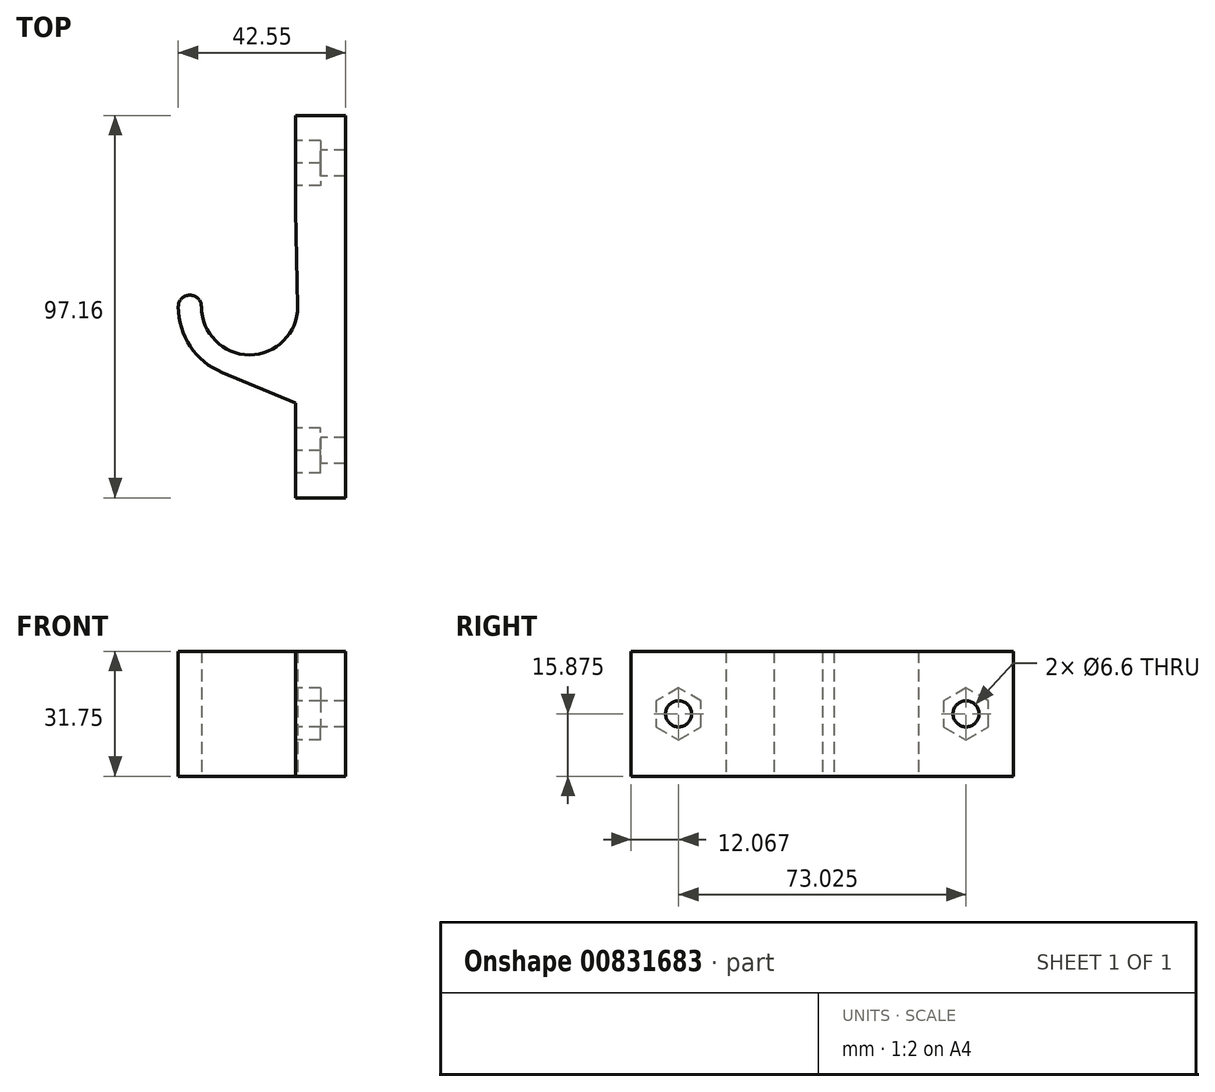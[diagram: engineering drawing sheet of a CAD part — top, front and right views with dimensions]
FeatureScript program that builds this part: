
annotation { "Feature Type Name" : "Feature", "Feature Type Description" : "" }
export const myFeature = defineFeature(function(context is Context, id is Id, definition is map)
    precondition{}
    {
        {
            assignVariable(context, id + "F0", {"name" : "materialThickness", "anyValue" : 6.35 * mm});
        }
        {
            assignVariable(context, id + "F1", {"name" : "overallThickness", "anyValue" : 31.75 * mm});
        }
        {
            var Q0;
            Q0=qCreatedBy(makeId("Top.planeOp"),FACE);
            var sketch = newSketch(context, id + "F2", { "sketchPlane" : qUnion([Q0])});
            skCircle(sketch, "E0", {"center": v(0, 0) * mm, "radius": 11.75 * mm, "construction": true});
            skLineSegment(sketch, "E1", {"start": v(0, 0) * mm, "end": v(24.45, 0) * mm, "construction": true});
            skLineSegment(sketch, "E2", {"start": v(24.45, 48.58) * mm, "end": v(24.45, -48.58) * mm});
            skLineSegment(sketch, "E3", {"start": v(24.45, 48.58) * mm, "end": v(11.75, 48.58) * mm});
            skLineSegment(sketch, "E4", {"start": v(24.45, -48.58) * mm, "end": v(11.75, -48.58) * mm});
            skLineSegment(sketch, "E5", {"start": v(11.75, 48.58) * mm, "end": v(11.75, 24.45) * mm});
            skLineSegment(sketch, "E6", {"start": v(11.75, -48.58) * mm, "end": v(11.75, -24.45) * mm});
            skCircle(sketch, "E7", {"center": v(0, 0) * mm, "radius": 18.1 * mm, "construction": true});
            skLineSegment(sketch, "E8", {"start": v(11.75, -24.45) * mm, "end": v(-6.92, -16.73) * mm});
            skLineSegment(sketch, "E9", {"start": v(11.75, 24.45) * mm, "end": v(12.22, 0) * mm});
            skLineSegment(sketch, "E10", {"start": v(0, 0) * mm, "end": v(-18.1, 0) * mm, "construction": true});
            skArc(sketch, "E11", {"start": v(12.22, 0) * mm, "mid": v(0, -12.22) * mm, "end": v(-12.22, 0) * mm});
            skArc(sketch, "E12", {"start": v(-6.92, -16.73) * mm, "mid": v(-15.05, -10.06) * mm, "end": v(-18.1, 0) * mm});
            skArc(sketch, "E13", {"start": v(-12.22, 0) * mm, "mid": v(-15.16, 2.94) * mm, "end": v(-18.1, 0) * mm});
            skSolve(sketch);
        }
        {
            var Q0;
            Q0=makeQuery(id+"F2.imprint","IMPRINT",FACE,{"disambiguationData":[TD([[makeQuery(id+"F2.imprint","IMPRINT",EDGE,{"derivedFrom":sQuery(id+"F2.wireOp",EDGE,"E2")}),-1.0]])]});
            extrude(context, id + "F3", {"entities" : qUnion([Q0]), "depth" : getVariable(context, 'overallThickness'), "offsetDistance" : 25.4 * mm});
        }
        {
            var Q0;
            Q0=makeQuery(id+"F3.opExtrude","SWEPT_FACE",FACE,{"disambiguationData":[OSD([sQuery(id+"F2.wireOp",EDGE,"E5"),sQuery(id+"F2.wireOp",EDGE,"E9")])]});
            var sketch = newSketch(context, id + "F4", { "sketchPlane" : qUnion([Q0])});
            skLineSegment(sketch, "E14.0", {"start": v(-48.58, 31.75) * mm, "end": v(-24.45, 31.75) * mm, "construction": true});
            skLineSegment(sketch, "E15.0", {"start": v(-48.58, 31.75) * mm, "end": v(-48.58, 0) * mm, "construction": true});
            skLineSegment(sketch, "E16.0", {"start": v(-48.58, 0) * mm, "end": v(-24.45, 0) * mm, "construction": true});
            skLineSegment(sketch, "E17.0", {"start": v(48.58, 31.75) * mm, "end": v(24.45, 31.75) * mm, "construction": true});
            skLineSegment(sketch, "E18.0", {"start": v(48.58, 31.75) * mm, "end": v(48.58, 0) * mm, "construction": true});
            skLineSegment(sketch, "E19.0", {"start": v(48.58, 0) * mm, "end": v(24.45, 0) * mm, "construction": true});
            skLineSegment(sketch, "E20", {"start": v(-48.58, 15.88) * mm, "end": v(48.58, 15.88) * mm, "construction": true});
            skPoint(sketch, "E21", {"position": v(-36.51, 15.88) * mm});
            skPoint(sketch, "E22", {"position": v(36.51, 15.88) * mm});
            skCircle(sketch, "E23", {"center": v(36.51, 15.88) * mm, "radius": 3.3 * mm});
            skCircle(sketch, "E24", {"center": v(-36.51, 15.88) * mm, "radius": 3.3 * mm});
            skCircle(sketch, "E25.cCircle", {"center": v(-36.51, 15.88) * mm, "radius": 5.72 * mm, "construction": true});
            skLineSegment(sketch, "E25.0", {"start": v(-30.8, 19.17) * mm, "end": v(-30.8, 12.58) * mm});
            skLineSegment(sketch, "E25.1", {"start": v(-30.8, 12.58) * mm, "end": v(-36.51, 9.28) * mm});
            skLineSegment(sketch, "E25.2", {"start": v(-36.51, 9.28) * mm, "end": v(-42.23, 12.58) * mm});
            skLineSegment(sketch, "E25.3", {"start": v(-42.23, 12.58) * mm, "end": v(-42.23, 19.17) * mm});
            skLineSegment(sketch, "E25.4", {"start": v(-42.23, 19.17) * mm, "end": v(-36.51, 22.47) * mm});
            skLineSegment(sketch, "E25.5", {"start": v(-36.51, 22.47) * mm, "end": v(-30.8, 19.17) * mm});
            skPoint(sketch, "E25.0.midPoint", {"position": v(-30.8, 15.88) * mm});
            skCircle(sketch, "E26.cCircle", {"center": v(36.51, 15.88) * mm, "radius": 5.72 * mm, "construction": true});
            skLineSegment(sketch, "E26.0", {"start": v(30.8, 12.58) * mm, "end": v(30.8, 19.17) * mm});
            skLineSegment(sketch, "E26.1", {"start": v(30.8, 19.17) * mm, "end": v(36.51, 22.47) * mm});
            skLineSegment(sketch, "E26.2", {"start": v(36.51, 22.47) * mm, "end": v(42.23, 19.17) * mm});
            skLineSegment(sketch, "E26.3", {"start": v(42.23, 19.17) * mm, "end": v(42.23, 12.58) * mm});
            skLineSegment(sketch, "E26.4", {"start": v(42.23, 12.58) * mm, "end": v(36.51, 9.28) * mm});
            skLineSegment(sketch, "E26.5", {"start": v(36.51, 9.28) * mm, "end": v(30.8, 12.58) * mm});
            skPoint(sketch, "E26.0.midPoint", {"position": v(30.8, 15.88) * mm});
            skSolve(sketch);
        }
        {
            var Q0;
            Q0=makeQuery(id+"F4.imprint","IMPRINT",FACE,{"disambiguationData":[TD([[makeQuery(id+"F4.imprint","IMPRINT",EDGE,{"derivedFrom":sQuery(id+"F4.wireOp",EDGE,"E24")}),1.0]])]});
            var Q1;
            Q1=makeQuery(id+"F4.imprint","IMPRINT",FACE,{"disambiguationData":[TD([[makeQuery(id+"F4.imprint","IMPRINT",EDGE,{"derivedFrom":sQuery(id+"F4.wireOp",EDGE,"E23")}),1.0]])]});
            var Q2;
            Q2=makeQuery(id+"F3.opExtrude","SWEPT_FACE",FACE,{"disambiguationData":[OSD([sQuery(id+"F2.wireOp",EDGE,"E2")])]});
            extrude(context, id + "F5", {"entities" : qUnion([Q0, Q1]), "operationType" : NewBodyOperationType.REMOVE, "endBound" : BoundingType.UP_TO_SURFACE, "oppositeDirection" : true, "depth" : 25.4 * mm, "endBoundEntityFace" : qUnion([Q2]), "offsetDistance" : 25.4 * mm});
        }
        {
            var Q0;
            Q0=makeQuery(id+"F4.imprint","IMPRINT",FACE,{"disambiguationData":[TD([[makeQuery(id+"F4.imprint","IMPRINT",EDGE,{"derivedFrom":sQuery(id+"F4.wireOp",EDGE,"E24")}),-1.0]])]});
            var Q1;
            Q1=makeQuery(id+"F4.imprint","IMPRINT",FACE,{"disambiguationData":[TD([[makeQuery(id+"F4.imprint","IMPRINT",EDGE,{"derivedFrom":sQuery(id+"F4.wireOp",EDGE,"E23")}),-1.0]])]});
            extrude(context, id + "F6", {"entities" : qUnion([Q0, Q1]), "operationType" : NewBodyOperationType.REMOVE, "oppositeDirection" : true, "depth" : getVariable(context, 'materialThickness'), "offsetDistance" : 25.4 * mm});
        }
    });
